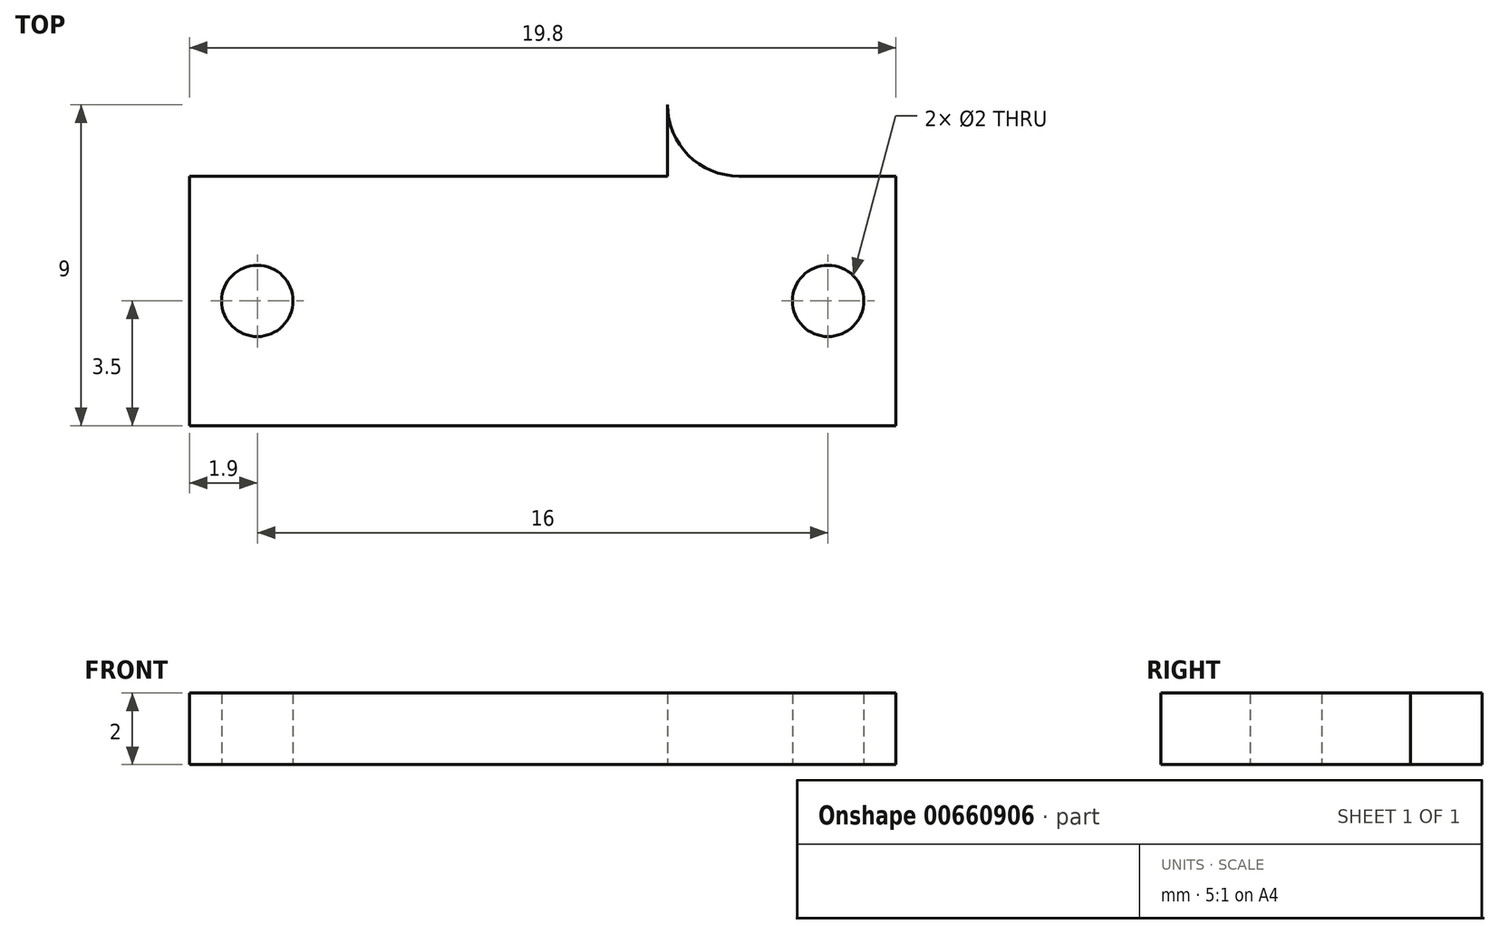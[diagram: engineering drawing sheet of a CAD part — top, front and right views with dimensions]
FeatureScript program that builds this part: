
annotation { "Feature Type Name" : "Feature", "Feature Type Description" : "" }
export const myFeature = defineFeature(function(context is Context, id is Id, definition is map)
    precondition{}
    {
        {
            var Q0;
            Q0=qCreatedBy(makeId("Top.planeOp"),FACE);
            var sketch = newSketch(context, id + "F0", { "sketchPlane" : qUnion([Q0])});
            skLineSegment(sketch, "E0.bottom", {"start": v(9.9, -3.5) * mm, "end": v(-9.9, -3.5) * mm});
            skLineSegment(sketch, "E0.top", {"start": v(9.9, 3.5) * mm, "end": v(-9.9, 3.5) * mm});
            skLineSegment(sketch, "E0.left", {"start": v(9.9, -3.5) * mm, "end": v(9.9, 3.5) * mm});
            skLineSegment(sketch, "E0.right", {"start": v(-9.9, -3.5) * mm, "end": v(-9.9, 3.5) * mm});
            skPoint(sketch, "E0.middle", {"position": v(0, 0) * mm});
            skPoint(sketch, "E1", {"position": v(-8, 0) * mm});
            skPoint(sketch, "E2.MirrorP", {"position": v(8, 0) * mm});
            skLineSegment(sketch, "E3.bottom", {"start": v(-3.5, 3.5) * mm, "end": v(3.5, 3.5) * mm});
            skLineSegment(sketch, "E3.top", {"start": v(-3.5, 12.5) * mm, "end": v(3.5, 12.5) * mm});
            skLineSegment(sketch, "E3.left", {"start": v(-3.5, 3.5) * mm, "end": v(-3.5, 12.5) * mm});
            skLineSegment(sketch, "E3.right", {"start": v(3.5, 3.5) * mm, "end": v(3.5, 12.5) * mm});
            skPoint(sketch, "E3.middle", {"position": v(0, 8) * mm});
            skLineSegment(sketch, "E4.bottom", {"start": v(-3.5, 3.5) * mm, "end": v(-5.5, 3.5) * mm, "construction": true});
            skLineSegment(sketch, "E4.top", {"start": v(-3.5, 5.5) * mm, "end": v(-5.5, 5.5) * mm, "construction": true});
            skLineSegment(sketch, "E4.left", {"start": v(-3.5, 3.5) * mm, "end": v(-3.5, 5.5) * mm, "construction": true});
            skLineSegment(sketch, "E4.right", {"start": v(-5.5, 3.5) * mm, "end": v(-5.5, 5.5) * mm, "construction": true});
            skArc(sketch, "E5", {"start": v(-3.5, 5.5) * mm, "mid": v(-4.09, 4.09) * mm, "end": v(-5.5, 3.5) * mm});
            skArc(sketch, "E6.MirrorCS", {"start": v(3.5, 5.5) * mm, "mid": v(4.09, 4.09) * mm, "end": v(5.5, 3.5) * mm});
            skSolve(sketch);
        }
        {
            var Q0;
            Q0=makeQuery(id+"F0.imprint","IMPRINT",FACE,{"disambiguationData":[TD([[makeQuery(id+"F0.imprint","IMPRINT",EDGE,{"derivedFrom":sQuery(id+"F0.wireOp",EDGE,"E0.bottom")}),-1.0]])]});
            var Q1;
            Q1=makeQuery(id+"F0.imprint","IMPRINT",FACE,{"disambiguationData":[TD([[makeQuery(id+"F0.imprint","IMPRINT",EDGE,{"derivedFrom":sQuery(id+"F0.wireOp",EDGE,"E3.bottom")}),1.0]])]});
            var Q2;
            {var subQ3=sQuery(id+"F0.wireOp",EDGE,"E5");Q2=makeQuery(id+"F0.imprint","IMPRINT",FACE,{"disambiguationData":[TD([[makeQuery(id+"F0.imprint","IMPRINT",EDGE,{"derivedFrom":subQ3}),1.0]])]});}
            var Q3;
            {var subQ3=sQuery(id+"F0.wireOp",EDGE,"E6.MirrorCS");Q3=makeQuery(id+"F0.imprint","IMPRINT",FACE,{"disambiguationData":[TD([[makeQuery(id+"F0.imprint","IMPRINT",EDGE,{"derivedFrom":subQ3}),-1.0]])]});}
            extrude(context, id + "F1", {"entities" : qUnion([Q0, Q1, Q2, Q3]), "depth" : 2 * mm, "offsetDistance" : 25 * mm});
        }
        {
            var Q0;
            Q0=sQuery(id+"F0.wireOp",VERTEX,"E1");
            var Q1;
            Q1=sQuery(id+"F0.wireOp",VERTEX,"E2.MirrorP");
            var Q2;
            Q2=makeQuery(id+"F1.opExtrude","SWEPT_BODY",BODY,{"disambiguationData":[OSD([sQuery(id+"F0.wireOp",EDGE,"E0.bottom"),sQuery(id+"F0.wireOp",EDGE,"E0.top"),sQuery(id+"F0.wireOp",EDGE,"E0.left"),sQuery(id+"F0.wireOp",EDGE,"E0.right")])]});
            hole(context, id + "F2", {"style" : HoleStyle.SIMPLE, "endStyle" : HoleEndStyle.THROUGH, "oppositeDirection" : true, "holeDiameter" : 2 * mm, "majorDiameter" : 5 * mm, "isTappedThrough" : true, "tappedDepth" : 12 * mm, "tapClearance" : 3, "locations" : qUnion([Q0, Q1]), "scope" : qUnion([Q2])});
        }
    });
